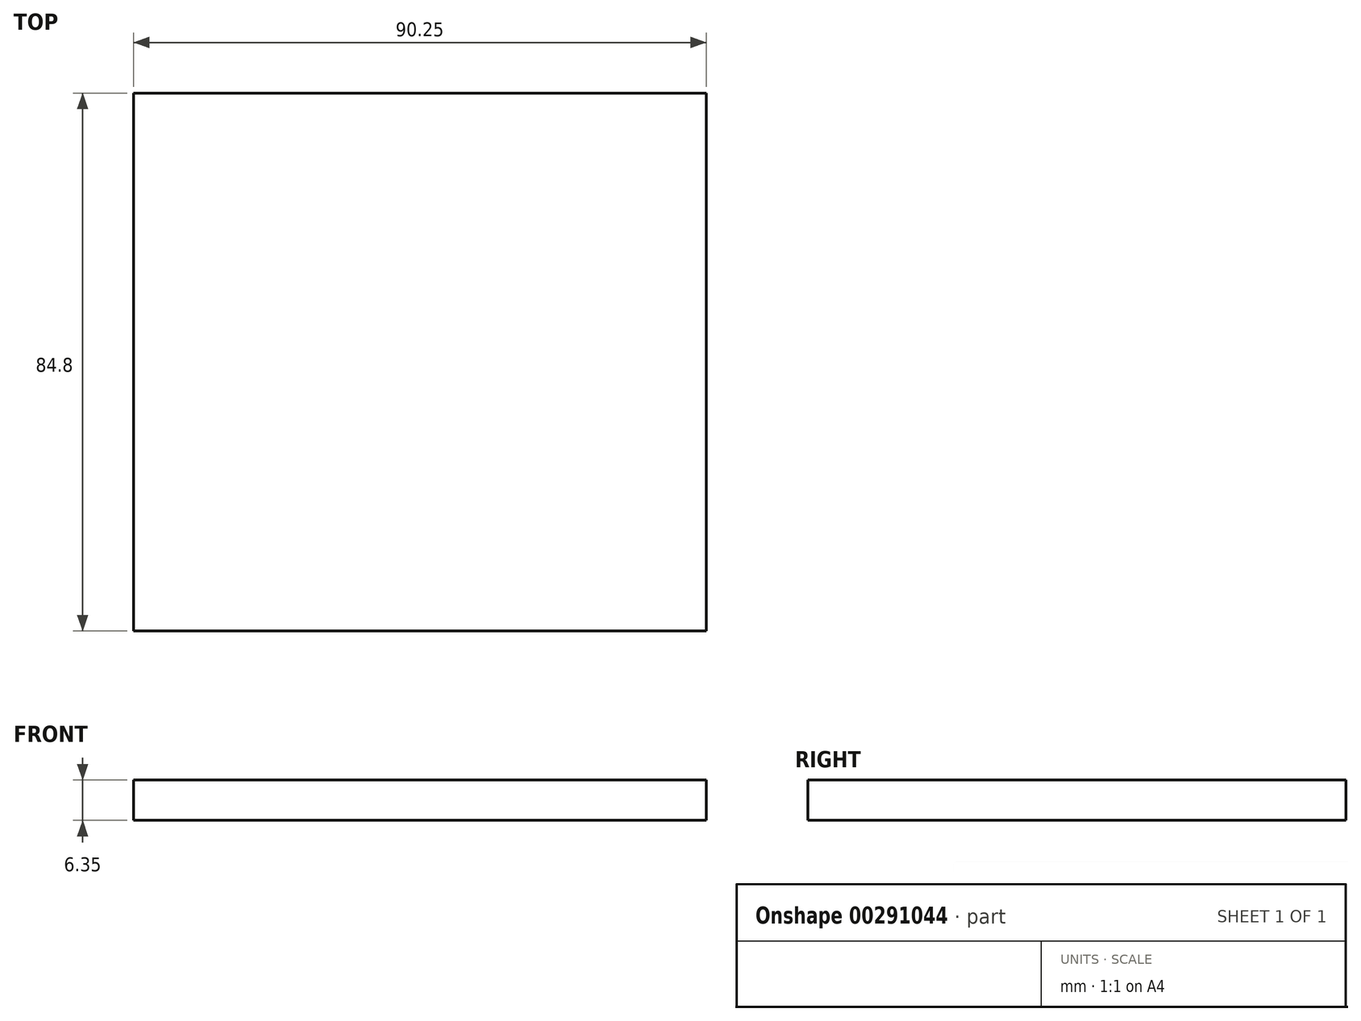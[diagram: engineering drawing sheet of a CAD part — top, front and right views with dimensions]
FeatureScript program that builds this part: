
annotation { "Feature Type Name" : "Feature", "Feature Type Description" : "" }
export const myFeature = defineFeature(function(context is Context, id is Id, definition is map)
    precondition{}
    {
        {
            var Q0;
            Q0=qCreatedBy(makeId("Top.planeOp"),FACE);
            var sketch = newSketch(context, id + "F0", { "sketchPlane" : qUnion([Q0])});
            skLineSegment(sketch, "E0.bottom", {"start": v(-44.15, 13.9) * mm, "end": v(46.1, 13.9) * mm});
            skLineSegment(sketch, "E0.top", {"start": v(-44.15, -70.9) * mm, "end": v(46.1, -70.9) * mm});
            skLineSegment(sketch, "E0.left", {"start": v(-44.15, 13.9) * mm, "end": v(-44.15, -70.9) * mm});
            skLineSegment(sketch, "E0.right", {"start": v(46.1, 13.9) * mm, "end": v(46.1, -70.9) * mm});
            skLineSegment(sketch, "E1", {"start": v(-112.1, 125.3) * mm, "end": v(-112.1, -77.9) * mm});
            skSolve(sketch);
        }
        {
            var Q0;
            Q0=makeQuery(id+"F0.imprint","IMPRINT",FACE,{"disambiguationData":[TD([[makeQuery(id+"F0.imprint","IMPRINT",EDGE,{"derivedFrom":sQuery(id+"F0.wireOp",EDGE,"E0.bottom")}),-1.0]])]});
            extrude(context, id + "F1", {"entities" : qUnion([Q0]), "depth" : 6.35 * mm});
        }
    });
